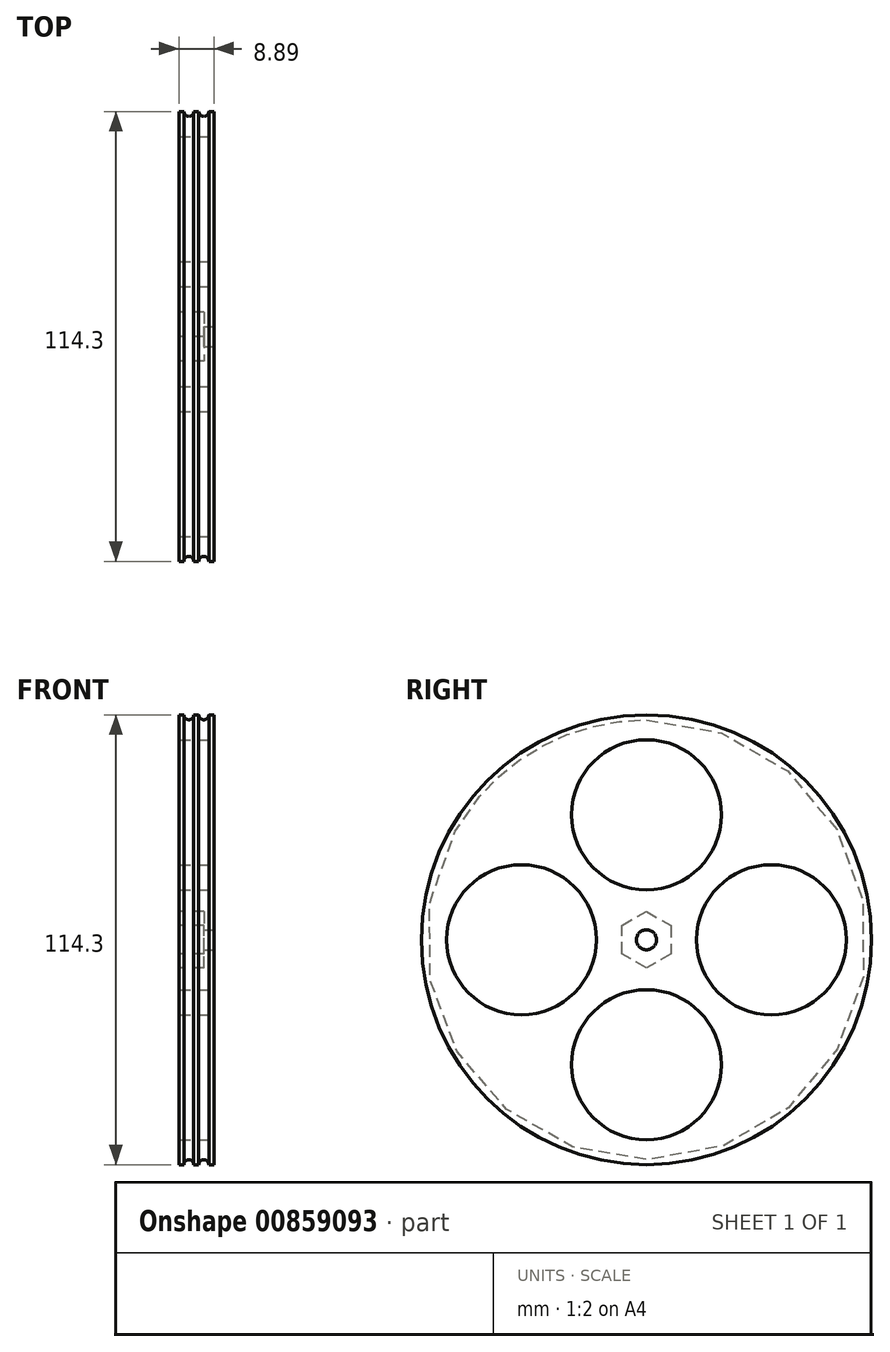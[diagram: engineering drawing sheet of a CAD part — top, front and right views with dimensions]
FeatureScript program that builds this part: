
annotation { "Feature Type Name" : "Feature", "Feature Type Description" : "" }
export const myFeature = defineFeature(function(context is Context, id is Id, definition is map)
    precondition{}
    {
        {
            var Q0;
            Q0=qCreatedBy(makeId("Front.planeOp"),FACE);
            var sketch = newSketch(context, id + "F0", { "sketchPlane" : qUnion([Q0])});
            skLineSegment(sketch, "E0.bottom", {"start": v(0, 0) * mm, "end": v(8.9, 0) * mm});
            skLineSegment(sketch, "E0.top", {"start": v(0, 57.15) * mm, "end": v(8.89, 57.15) * mm});
            skLineSegment(sketch, "E0.left", {"start": v(0, 0) * mm, "end": v(0, 57.15) * mm});
            skLineSegment(sketch, "E0.right", {"start": v(8.9, 0) * mm, "end": v(8.89, 57.15) * mm});
            skCircle(sketch, "E1", {"center": v(2.54, 57.15) * mm, "radius": 1.27 * mm});
            skCircle(sketch, "E2", {"center": v(6.35, 57.15) * mm, "radius": 1.27 * mm});
            skSolve(sketch);
        }
        {
            var Q0;
            Q0=makeQuery(id+"F0.imprint","IMPRINT",FACE,{"disambiguationData":[TD([[makeQuery(id+"F0.imprint","IMPRINT",EDGE,{"derivedFrom":sQuery(id+"F0.wireOp",EDGE,"E0.bottom")}),1.0]])]});
            var Q1;
            Q1=sQuery(id+"F0.wireOp",EDGE,"E0.bottom");
            revolve(context, id + "F1", {"surfaceOperationType" : NewSurfaceOperationType.NEW, "entities" : qUnion([Q0]), "axis" : qUnion([Q1]), "revolveType" : RevolveType.FULL});
        }
        {
            var Q0;
            Q0=makeQuery(id+"F1.opRevolve","SWEPT_FACE",FACE,{"disambiguationData":[OSD([sQuery(id+"F0.wireOp",EDGE,"E0.right")])]});
            var sketch = newSketch(context, id + "F2", { "sketchPlane" : qUnion([Q0])});
            skCircle(sketch, "E3", {"center": v(0, 0) * mm, "radius": 12.7 * mm});
            skSolve(sketch);
        }
        {
            var Q0;
            Q0=makeQuery(id+"F2.imprint","IMPRINT",FACE,{"disambiguationData":[TD([[makeQuery(id+"F2.imprint","IMPRINT",EDGE,{"derivedFrom":sQuery(id+"F2.wireOp",EDGE,"E3")}),-1.0]])]});
            var sketch = newSketch(context, id + "F3", { "sketchPlane" : qUnion([Q0])});
            skCircle(sketch, "E4", {"center": v(-31.75, 0) * mm, "radius": 19.05 * mm});
            skCircle(sketch, "E5.1.0", {"center": v(0, 31.75) * mm, "radius": 19.05 * mm});
            skCircle(sketch, "E5.2.0", {"center": v(31.75, 0) * mm, "radius": 19.05 * mm});
            skCircle(sketch, "E5.3.0", {"center": v(0, -31.75) * mm, "radius": 19.05 * mm});
            skPoint(sketch, "E5.center", {"position": v(0, 0) * mm});
            skLineSegment(sketch, "E5.anchor1", {"start": v(0, 0) * mm, "end": v(-31.75, 0) * mm, "construction": true});
            skLineSegment(sketch, "E5.anchor2", {"start": v(0, 0) * mm, "end": v(0, -31.75) * mm, "construction": true});
            skSolve(sketch);
        }
        {
            var Q0;
            Q0 = qSketchRegion(id + "F3", true);
            extrude(context, id + "F4", {"entities" : qUnion([Q0]), "operationType" : NewBodyOperationType.REMOVE, "oppositeDirection" : true, "depth" : 19.05 * mm, "offsetDistance" : 25.4 * mm});
        }
        {
            var Q0;
            Q0=qCreatedBy(makeId("Right.planeOp"),FACE);
            var sketch = newSketch(context, id + "F5", { "sketchPlane" : qUnion([Q0])});
            skCircle(sketch, "E6.cCircle", {"center": v(0, 0) * mm, "radius": 6.22 * mm, "construction": true});
            skLineSegment(sketch, "E6.0", {"start": v(-6.22, -3.6) * mm, "end": v(-6.22, 3.6) * mm});
            skLineSegment(sketch, "E6.1", {"start": v(-6.22, 3.6) * mm, "end": v(0, 7.19) * mm});
            skLineSegment(sketch, "E6.2", {"start": v(0, 7.19) * mm, "end": v(6.22, 3.6) * mm});
            skLineSegment(sketch, "E6.3", {"start": v(6.22, 3.6) * mm, "end": v(6.22, -3.6) * mm});
            skLineSegment(sketch, "E6.4", {"start": v(6.22, -3.6) * mm, "end": v(0, -7.19) * mm});
            skLineSegment(sketch, "E6.5", {"start": v(0, -7.19) * mm, "end": v(-6.22, -3.6) * mm});
            skPoint(sketch, "E6.0.midPoint", {"position": v(-6.22, 0) * mm});
            skSolve(sketch);
        }
        {
            var Q0;
            Q0=makeQuery(id+"F5.imprint","IMPRINT",FACE,{"disambiguationData":[TD([[makeQuery(id+"F5.imprint","IMPRINT",EDGE,{"derivedFrom":sQuery(id+"F5.wireOp",EDGE,"E6.0")}),-1.0]])]});
            extrude(context, id + "F6", {"entities" : qUnion([Q0]), "operationType" : NewBodyOperationType.REMOVE, "depth" : 6.35 * mm, "offsetDistance" : 25.4 * mm});
        }
        {
            var Q0;
            Q0=makeQuery(id+"F2.imprint","IMPRINT",FACE,{"disambiguationData":[TD([[makeQuery(id+"F2.imprint","IMPRINT",EDGE,{"derivedFrom":sQuery(id+"F2.wireOp",EDGE,"E3")}),1.0]])]});
            var sketch = newSketch(context, id + "F7", { "sketchPlane" : qUnion([Q0])});
            skCircle(sketch, "E7", {"center": v(0, 0) * mm, "radius": 2.54 * mm});
            skSolve(sketch);
        }
        {
            var Q0;
            Q0 = qSketchRegion(id + "F7", true);
            extrude(context, id + "F8", {"entities" : qUnion([Q0]), "operationType" : NewBodyOperationType.REMOVE, "endBound" : BoundingType.THROUGH_ALL, "oppositeDirection" : true, "depth" : 19.05 * mm, "offsetDistance" : 25.4 * mm});
        }
    });
